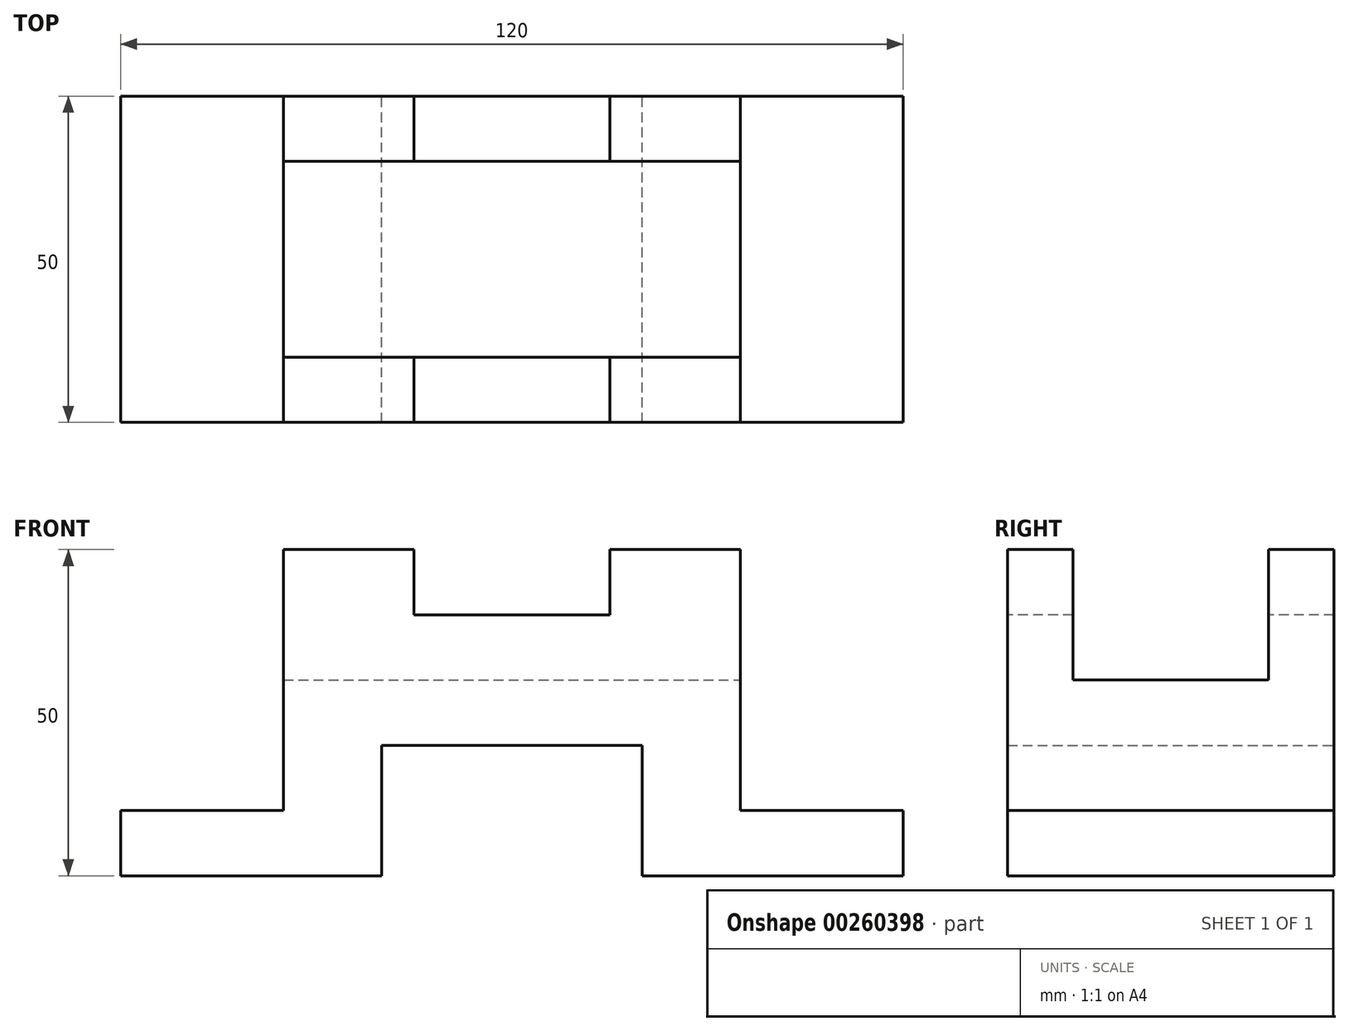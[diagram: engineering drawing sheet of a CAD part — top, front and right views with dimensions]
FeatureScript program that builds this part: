
annotation { "Feature Type Name" : "Feature", "Feature Type Description" : "" }
export const myFeature = defineFeature(function(context is Context, id is Id, definition is map)
    precondition{}
    {
        {
            assignVariable(context, id + "F0", {"name" : "B", "anyValue" : 50});
        }
        {
            assignVariable(context, id + "F1", {"name" : "A", "anyValue" : 50});
        }
        {
            var Q0;
            Q0=qCreatedBy(makeId("Top.planeOp"),FACE);
            var sketch = newSketch(context, id + "F2", { "sketchPlane" : qUnion([Q0])});
            skLineSegment(sketch, "E0.bottom", {"start": v(60, -25) * mm, "end": v(-60, -25) * mm});
            skLineSegment(sketch, "E0.top", {"start": v(60, 25) * mm, "end": v(-60, 25) * mm});
            skLineSegment(sketch, "E0.left", {"start": v(60, -25) * mm, "end": v(60, 25) * mm});
            skLineSegment(sketch, "E0.right", {"start": v(-60, -25) * mm, "end": v(-60, 25) * mm});
            skPoint(sketch, "E0.middle", {"position": v(0, 0) * mm});
            skSolve(sketch);
        }
        {
            var Q0;
            Q0 = qSketchRegion(id + "F2", true);
            extrude(context, id + "F3", {"entities" : qUnion([Q0]), "depth" : (getVariable(context, 'B')) * mm});
        }
        {
            var Q0;
            Q0=makeQuery(id+"F3.opExtrude","CAP_FACE",FACE,{"disambiguationData":[OSD([sQuery(id+"F2.wireOp",EDGE,"E0.bottom"),sQuery(id+"F2.wireOp",EDGE,"E0.top"),sQuery(id+"F2.wireOp",EDGE,"E0.left"),sQuery(id+"F2.wireOp",EDGE,"E0.right")])],"isStart":false});
            var sketch = newSketch(context, id + "F4", { "sketchPlane" : qUnion([Q0])});
            skLineSegment(sketch, "E1.bottom", {"start": v(-60, 15) * mm, "end": v(60, 15) * mm});
            skLineSegment(sketch, "E1.top", {"start": v(-60, -15) * mm, "end": v(60, -15) * mm});
            skLineSegment(sketch, "E1.left", {"start": v(-60, 15) * mm, "end": v(-60, -15) * mm});
            skLineSegment(sketch, "E1.right", {"start": v(60, 15) * mm, "end": v(60, -15) * mm});
            skPoint(sketch, "E1.middle", {"position": v(0, 0) * mm});
            skSolve(sketch);
        }
        {
            var Q0;
            Q0=makeQuery(id+"F4.imprint","IMPRINT",FACE,{"disambiguationData":[TD([[makeQuery(id+"F4.imprint","IMPRINT",EDGE,{"derivedFrom":sQuery(id+"F4.wireOp",EDGE,"E1.bottom")}),-1.0]])]});
            extrude(context, id + "F5", {"entities" : qUnion([Q0]), "operationType" : NewBodyOperationType.REMOVE, "oppositeDirection" : true, "depth" : 20 * mm});
        }
        {
            var Q0;
            Q0=makeQuery(id+"F3.opExtrude","CAP_FACE",FACE,{"disambiguationData":[OSD([sQuery(id+"F2.wireOp",EDGE,"E0.bottom"),sQuery(id+"F2.wireOp",EDGE,"E0.top"),sQuery(id+"F2.wireOp",EDGE,"E0.left"),sQuery(id+"F2.wireOp",EDGE,"E0.right")])],"isStart":true});
            var sketch = newSketch(context, id + "F6", { "sketchPlane" : qUnion([Q0])});
            skLineSegment(sketch, "E2.bottom", {"start": v(20, 25) * mm, "end": v(-20, 25) * mm});
            skLineSegment(sketch, "E2.top", {"start": v(20, -25) * mm, "end": v(-20, -25) * mm});
            skLineSegment(sketch, "E2.left", {"start": v(20, 25) * mm, "end": v(20, -25) * mm});
            skLineSegment(sketch, "E2.right", {"start": v(-20, 25) * mm, "end": v(-20, -25) * mm});
            skPoint(sketch, "E2.middle", {"position": v(0, 0) * mm});
            skSolve(sketch);
        }
        {
            var Q0;
            Q0 = qSketchRegion(id + "F6", true);
            extrude(context, id + "F7", {"entities" : qUnion([Q0]), "operationType" : NewBodyOperationType.REMOVE, "oppositeDirection" : true, "depth" : 20 * mm});
        }
        {
            var Q0;
            Q0=makeQuery(id+"F3.opExtrude","SWEPT_FACE",FACE,{"disambiguationData":[OSD([sQuery(id+"F2.wireOp",EDGE,"E0.bottom")])]});
            var sketch = newSketch(context, id + "F8", { "sketchPlane" : qUnion([Q0])});
            skLineSegment(sketch, "E3.bottom", {"start": v(-60, 50) * mm, "end": v(-35, 50) * mm});
            skLineSegment(sketch, "E3.top", {"start": v(-60, 10) * mm, "end": v(-35, 10) * mm});
            skLineSegment(sketch, "E3.left", {"start": v(-60, 50) * mm, "end": v(-60, 10) * mm});
            skLineSegment(sketch, "E3.right", {"start": v(-35, 50) * mm, "end": v(-35, 10) * mm});
            skSolve(sketch);
        }
        {
            var Q0;
            Q0 = qSketchRegion(id + "F8", true);
            extrude(context, id + "F9", {"entities" : qUnion([Q0]), "operationType" : NewBodyOperationType.REMOVE, "oppositeDirection" : true, "depth" : (getVariable(context, 'A')) * mm});
        }
        {
            var Q0;
            Q0=makeQuery(id+"F3.opExtrude","SWEPT_FACE",FACE,{"disambiguationData":[OSD([sQuery(id+"F2.wireOp",EDGE,"E0.bottom")])]});
            var sketch = newSketch(context, id + "F10", { "sketchPlane" : qUnion([Q0])});
            skLineSegment(sketch, "E4.bottom", {"start": v(60, 50) * mm, "end": v(35, 50) * mm});
            skLineSegment(sketch, "E4.top", {"start": v(60, 10) * mm, "end": v(35, 10) * mm});
            skLineSegment(sketch, "E4.left", {"start": v(60, 50) * mm, "end": v(60, 10) * mm});
            skLineSegment(sketch, "E4.right", {"start": v(35, 50) * mm, "end": v(35, 10) * mm});
            skSolve(sketch);
        }
        {
            var Q0;
            Q0 = qSketchRegion(id + "F10", true);
            extrude(context, id + "F11", {"entities" : qUnion([Q0]), "operationType" : NewBodyOperationType.REMOVE, "oppositeDirection" : true, "depth" : (getVariable(context, 'A')) * mm});
        }
        {
            var Q0;
            Q0=makeQuery(id+"F3.opExtrude","SWEPT_FACE",FACE,{"disambiguationData":[OSD([sQuery(id+"F2.wireOp",EDGE,"E0.bottom")])]});
            var sketch = newSketch(context, id + "F12", { "sketchPlane" : qUnion([Q0])});
            skLineSegment(sketch, "E5.bottom", {"start": v(-15, 40) * mm, "end": v(15, 40) * mm});
            skLineSegment(sketch, "E5.top", {"start": v(-15, 60) * mm, "end": v(15, 60) * mm});
            skLineSegment(sketch, "E5.left", {"start": v(-15, 40) * mm, "end": v(-15, 60) * mm});
            skLineSegment(sketch, "E5.right", {"start": v(15, 40) * mm, "end": v(15, 60) * mm});
            skPoint(sketch, "E5.middle", {"position": v(0, 50) * mm});
            skSolve(sketch);
        }
        {
            var Q0;
            Q0 = qSketchRegion(id + "F12", true);
            extrude(context, id + "F13", {"entities" : qUnion([Q0]), "operationType" : NewBodyOperationType.REMOVE, "oppositeDirection" : true, "depth" : (getVariable(context, 'A')) * mm});
        }
    });
